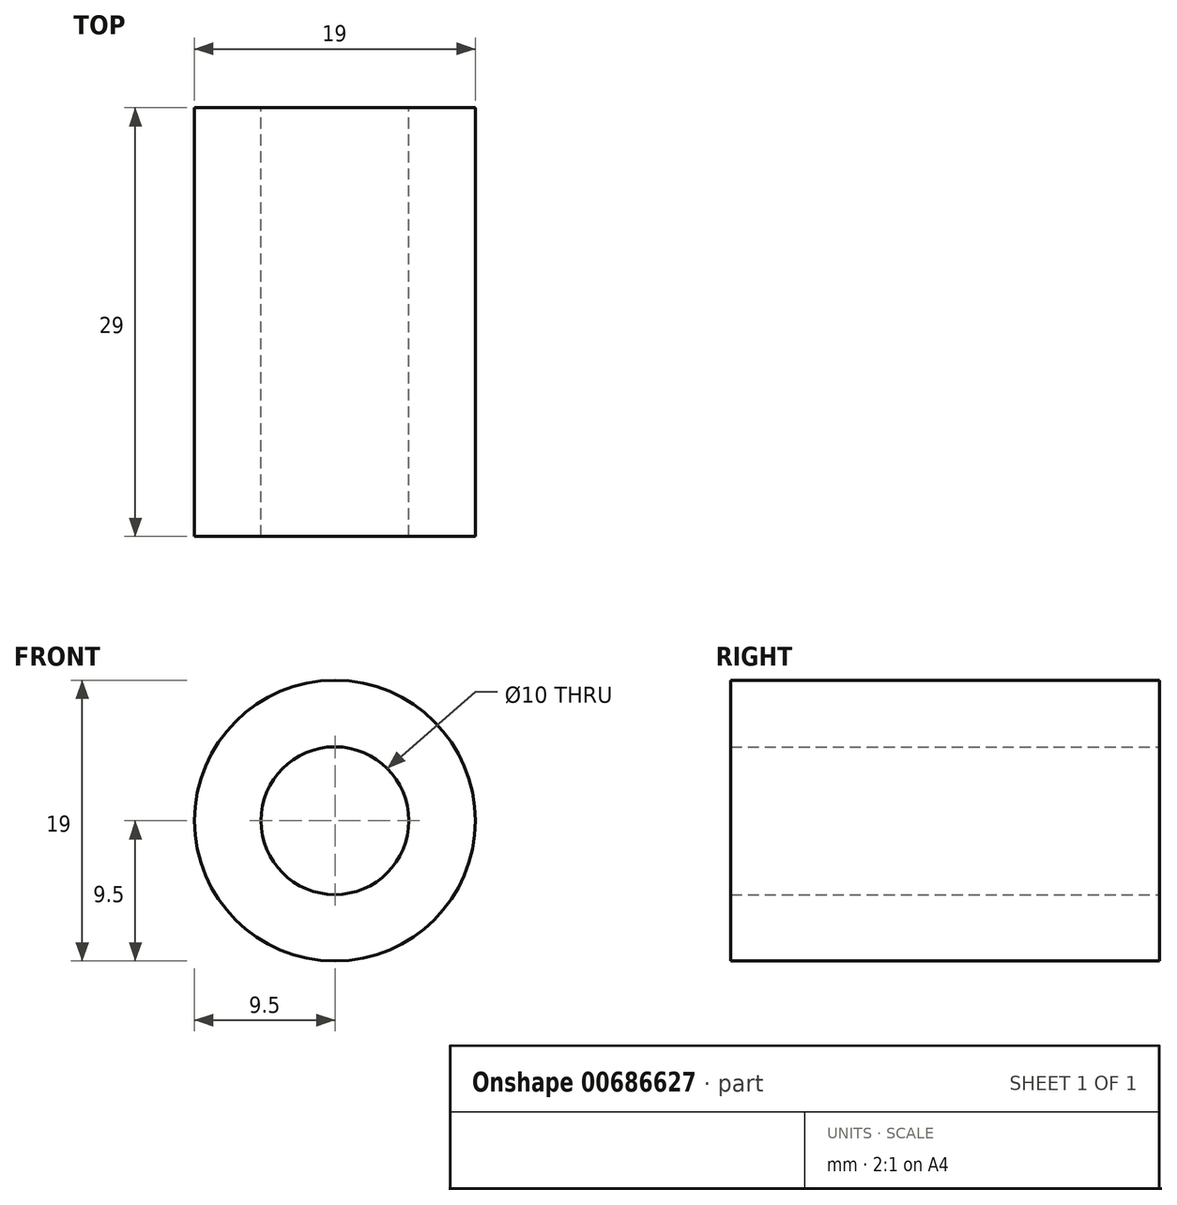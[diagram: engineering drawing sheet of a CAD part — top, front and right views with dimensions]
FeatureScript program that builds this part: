
annotation { "Feature Type Name" : "Feature", "Feature Type Description" : "" }
export const myFeature = defineFeature(function(context is Context, id is Id, definition is map)
    precondition{}
    {
        {
            var Q0;
            Q0=qCreatedBy(makeId("Front.planeOp"),FACE);
            var sketch = newSketch(context, id + "F0", { "sketchPlane" : qUnion([Q0])});
            skCircle(sketch, "E0", {"center": v(0, 0) * mm, "radius": 5 * mm});
            skCircle(sketch, "E1", {"center": v(0, 0) * mm, "radius": 9.5 * mm});
            skSolve(sketch);
        }
        {
            var Q0;
            Q0 = qSketchRegion(id + "F0", true);
            extrude(context, id + "F1", {"entities" : qUnion([Q0]), "depth" : 29 * mm, "offsetDistance" : 25 * mm});
        }
    });
